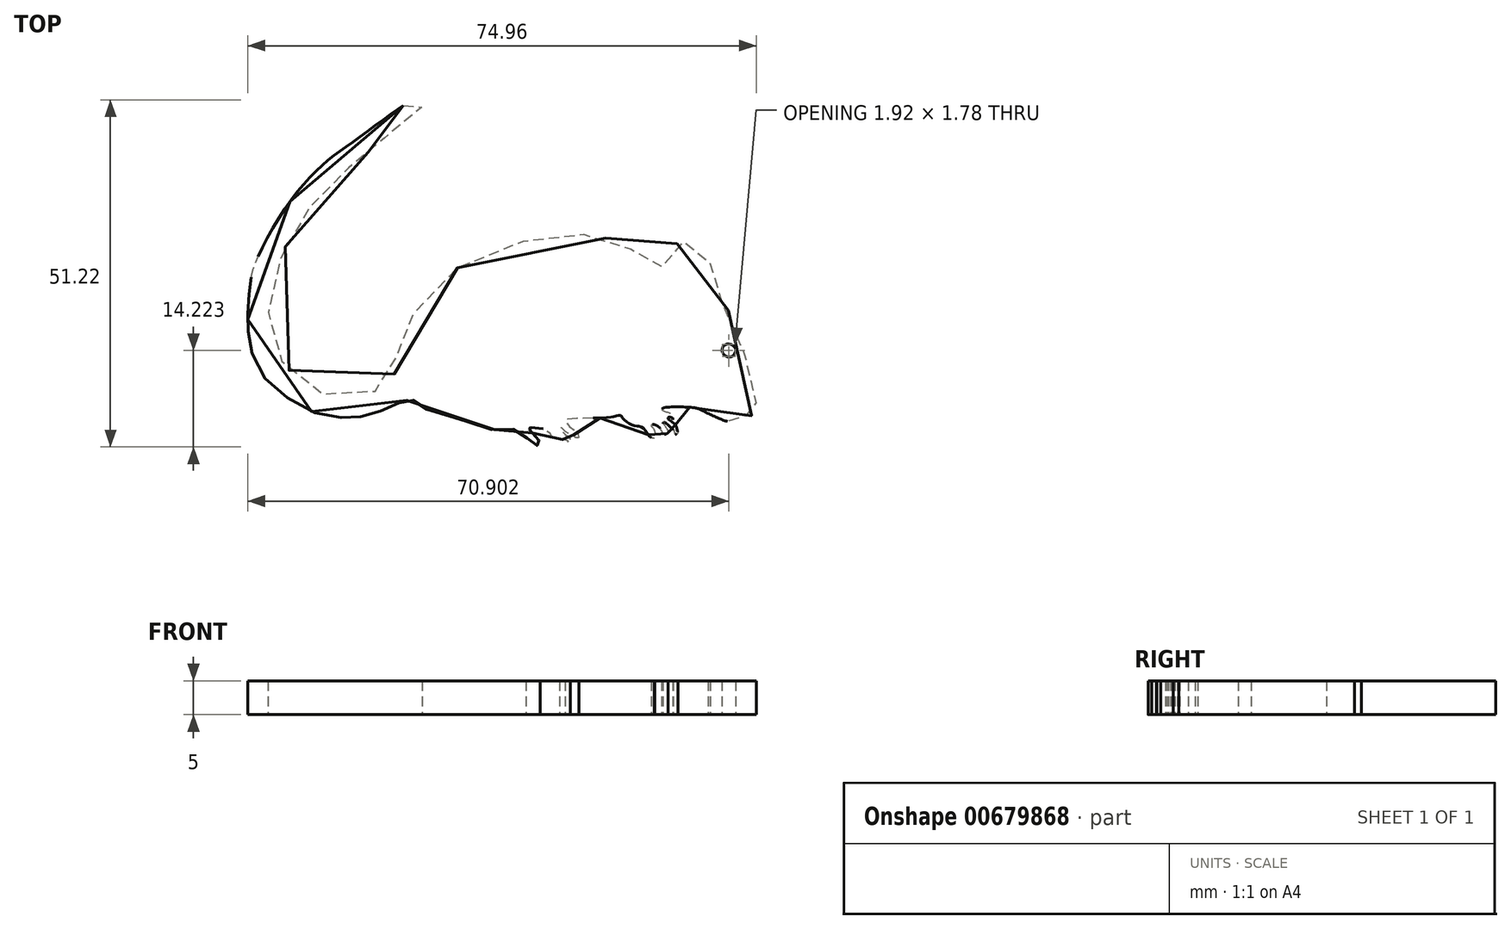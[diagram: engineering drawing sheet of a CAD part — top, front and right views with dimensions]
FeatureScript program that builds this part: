
annotation { "Feature Type Name" : "Feature", "Feature Type Description" : "" }
export const myFeature = defineFeature(function(context is Context, id is Id, definition is map)
    precondition{}
    {
        {
            var Q0;
            Q0=qCreatedBy(makeId("Top.planeOp"),FACE);
            var sketch = newSketch(context, id + "F0", { "sketchPlane" : qUnion([Q0])});
            skFitSpline(sketch, "E0", {"points": [v(-52.15, 62.47) * mm, v(-50.52, 63.22) * mm, v(-49.53, 63.22) * mm, v(-49.4, 62.28) * mm, v(-50.52, 61.22) * mm, v(-56.08, 56.73) * mm, v(-58.82, 54.36) * mm, v(-62.38, 51.5) * mm, v(-66.74, 46.38) * mm, v(-69.92, 40.76) * mm, v(-71.86, 33.96) * mm, v(-71.92, 29.85) * mm, v(-69.92, 24.54) * mm, v(-65.5, 20.67) * mm, v(-61.57, 19.43) * mm, v(-55.58, 20.67) * mm, v(-53.4, 23.1) * mm, v(-53.14, 26.48) * mm, v(-51.33, 30.6) * mm, v(-47.28, 36.27) * mm, v(-38.73, 41.07) * mm, v(-30.37, 43.32) * mm, v(-23.89, 43.26) * mm, v(-19.33, 41.76) * mm, v(-16.71, 39.76) * mm, v(-14.15, 38.45) * mm, v(-13.65, 40.64) * mm, v(-11.66, 42.13) * mm, v(-9.16, 42.45) * mm, v(-6.98, 40.51) * mm, v(-7.17, 35.9) * mm, v(-4.98, 33.09) * mm, v(-2.74, 29.28) * mm, v(-0.74, 20.61) * mm, v(-0.2, 18.76) * mm, v(-0.2, 17.38) * mm, v(-0.8, 16.72) * mm, v(-1.35, 16.65) * mm, v(-1.58, 16.75) * mm, v(-2.1, 16.38) * mm, v(-2.47, 16.16) * mm, v(-3.28, 15.93) * mm, v(-4.25, 15.84) * mm, v(-8.38, 17.62) * mm, v(-9.54, 17.93) * mm, v(-13.94, 17.8) * mm, v(-13.96, 17.53) * mm, v(-12.9, 17.14) * mm, v(-12.37, 16.56) * mm, v(-12.4, 16.05) * mm, v(-12.45, 16.34) * mm, v(-13.12, 16.43) * mm, v(-12.56, 15.82) * mm, v(-11.91, 15.18) * mm, v(-11.76, 14.6) * mm, v(-11.68, 14.2) * mm, v(-11.89, 14) * mm, v(-12.05, 14.03) * mm, v(-12.18, 14.55) * mm, v(-12.4, 14.73) * mm, v(-13.66, 15.77) * mm, v(-13.84, 15.72) * mm, v(-13.78, 15.52) * mm, v(-13.13, 14.53) * mm, v(-13.11, 14.23) * mm, v(-13.44, 14.02) * mm, v(-13.74, 13.98) * mm, v(-14.16, 14.65) * mm, v(-14.6, 15.15) * mm, v(-15.37, 15.44) * mm, v(-15.59, 15.26) * mm, v(-15.18, 14.73) * mm, v(-15.09, 14.03) * mm, v(-15.16, 13.66) * mm, v(-15.13, 13.42) * mm, v(-15.71, 13.52) * mm, v(-16.46, 14.57) * mm, v(-17.35, 15.16) * mm, v(-18, 15.23) * mm, v(-19.14, 15.76) * mm, v(-19.87, 16.47) * mm, v(-20.06, 16.74) * mm, v(-20.75, 16.7) * mm, v(-20.96, 16.65) * mm, v(-22.18, 16.45) * mm, v(-28.07, 16.2) * mm, v(-28.28, 16.09) * mm, v(-28.15, 15.76) * mm, v(-27.24, 14.74) * mm, v(-26.59, 14.39) * mm, v(-26.26, 13.7) * mm, v(-26.42, 13.39) * mm, v(-26.6, 13.37) * mm, v(-26.8, 13.77) * mm, v(-27.39, 13.95) * mm, v(-27.83, 14.11) * mm, v(-28.27, 14.38) * mm, v(-29, 15.02) * mm, v(-29.1, 14.91) * mm, v(-28.29, 13.96) * mm, v(-27.54, 13.24) * mm, v(-27.64, 12.63) * mm, v(-27.82, 12.85) * mm, v(-28.1, 13.16) * mm, v(-28.86, 13.18) * mm, v(-29.27, 13.18) * mm, v(-29.6, 13.2) * mm, v(-30.16, 13.45) * mm, v(-30.24, 13.73) * mm, v(-31.41, 14.77) * mm, v(-32.65, 15.06) * mm, v(-33.64, 15) * mm, v(-34.03, 15.08) * mm, v(-33.37, 14.51) * mm, v(-32.31, 13.26) * mm, v(-31.99, 12.82) * mm, v(-32.19, 12.1) * mm, v(-32.58, 12.52) * mm, v(-33.17, 12.9) * mm, v(-35.27, 14.4) * mm, v(-36.43, 14.72) * mm, v(-40.87, 14.96) * mm, v(-44.3, 16.57) * mm, v(-46.35, 16.69) * mm, v(-50.32, 18.7) * mm, v(-50.66, 18.99) * mm, v(-52, 18.89) * mm, v(-54, 18.06) * mm, v(-57.34, 16.75) * mm, v(-59.62, 16.49) * mm, v(-63.63, 16.64) * mm, v(-69.67, 19.69) * mm, v(-73.73, 24.01) * mm, v(-74.95, 28.56) * mm, v(-75.06, 30.41) * mm, v(-75.02, 33.56) * mm, v(-74.75, 35.58) * mm, v(-74.3, 38.3) * mm, v(-69.29, 47.71) * mm, v(-63.57, 54.12) * mm, v(-58.64, 57.79) * mm, v(-52.15, 62.47) * mm]});
            skFitSpline(sketch, "E1", {"points": [v(-4.68, 27.2) * mm, v(-5.08, 26.01) * mm, v(-3.8, 25.42) * mm, v(-3.2, 26.7) * mm, v(-4.68, 27.2) * mm]});
            skSolve(sketch);
        }
        {
            var Q0;
            Q0 = qSketchRegion(id + "F0", true);
            extrude(context, id + "F1", {"entities" : qUnion([Q0]), "depth" : 5 * mm, "offsetDistance" : 25.4 * mm});
        }
    });
